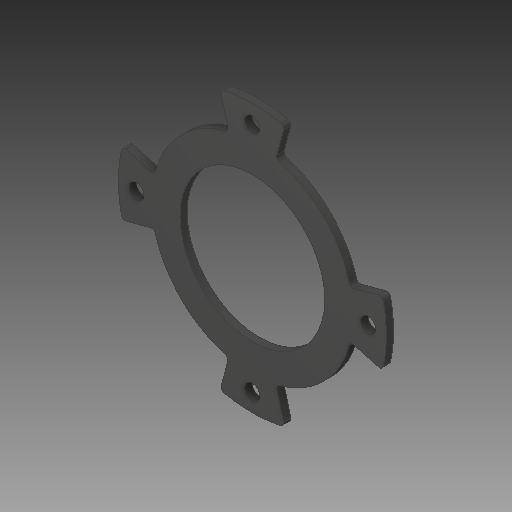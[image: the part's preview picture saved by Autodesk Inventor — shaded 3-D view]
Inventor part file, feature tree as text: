
AUTODESK INVENTOR PART (.ipt)
format: ipt  version: 2018 (Build 220112000, 112)  size: 133,632 bytes
history: native  units: in
note: dims shown in document units (in); Inventor stores cm internally (conversion verified against a paired STEP export)
features: fillet x1
ambient origin geometry x8: Origin, YZ Plane, XZ Plane, XY Plane, X Axis, Y Axis, Z Axis, Center Point
bodies: Solid1 (feature_tree)
feature tree (1):
  fillet  "Fillet1"  [1 undecoded]
note: 1 required parameter value undecoded (feature->parameter linkage not recoverable at this tier; creation-order binding heuristic only, values carry confidence <= 0.55)
